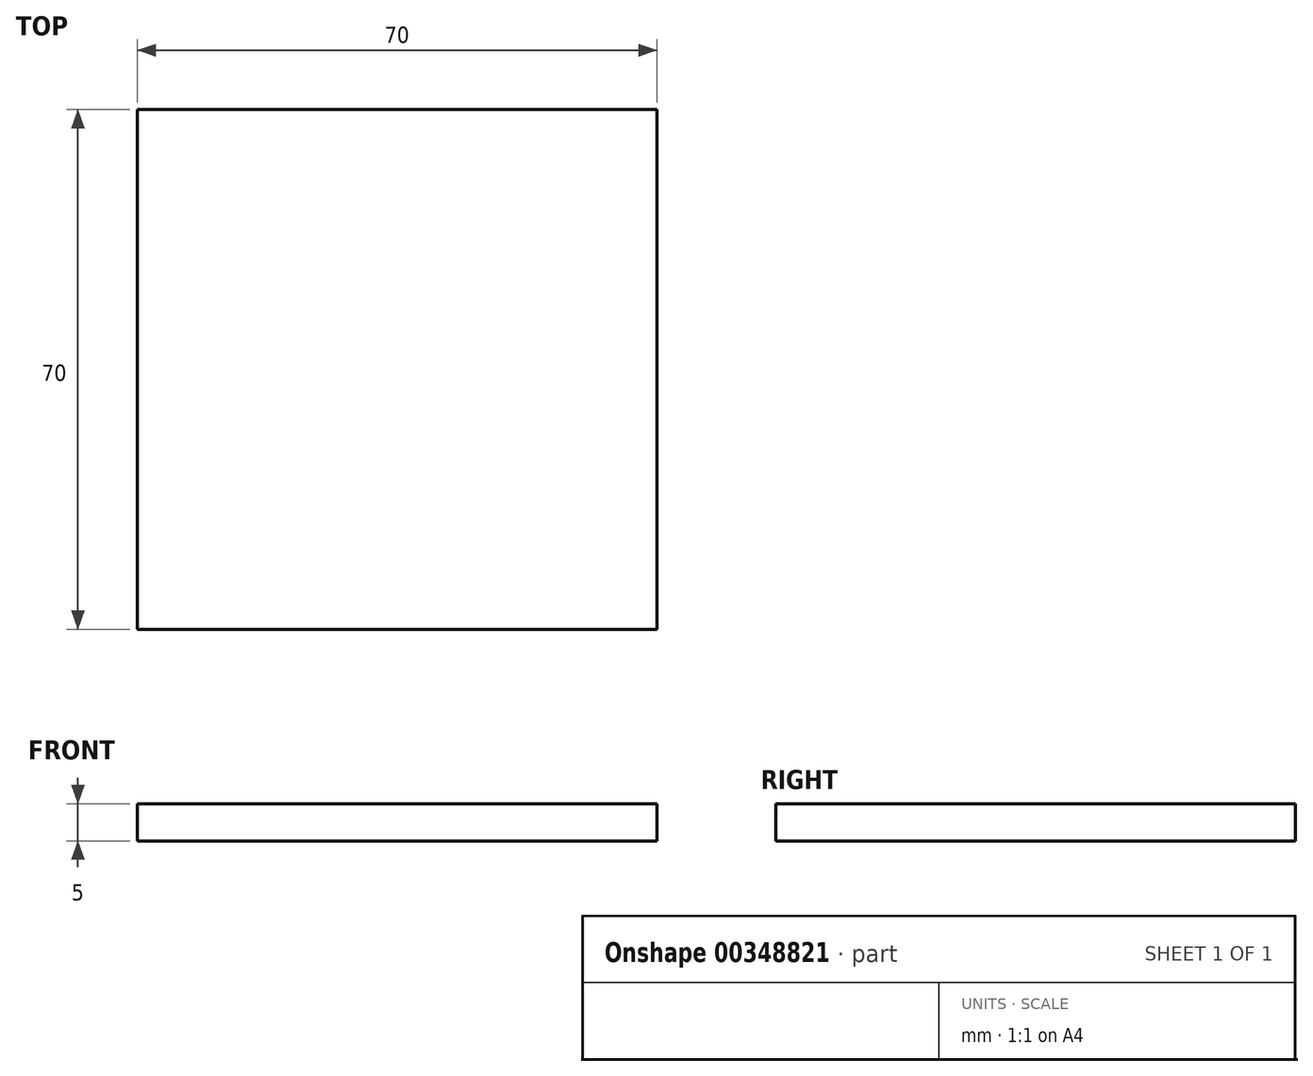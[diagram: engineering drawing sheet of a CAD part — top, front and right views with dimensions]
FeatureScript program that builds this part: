
annotation { "Feature Type Name" : "Feature", "Feature Type Description" : "" }
export const myFeature = defineFeature(function(context is Context, id is Id, definition is map)
    precondition{}
    {
        {
            var Q0;
            Q0=qCreatedBy(makeId("Top.planeOp"),FACE);
            var sketch = newSketch(context, id + "F0", { "sketchPlane" : qUnion([Q0])});
            skLineSegment(sketch, "E0.bottom", {"start": v(-35, 35) * mm, "end": v(35, 35) * mm});
            skLineSegment(sketch, "E0.top", {"start": v(-35, -35) * mm, "end": v(35, -35) * mm});
            skLineSegment(sketch, "E0.left", {"start": v(-35, 35) * mm, "end": v(-35, -35) * mm});
            skLineSegment(sketch, "E0.right", {"start": v(35, 35) * mm, "end": v(35, -35) * mm});
            skSolve(sketch);
        }
        {
            var Q0;
            Q0=makeQuery(id+"F0.imprint","IMPRINT",FACE,{"disambiguationData":[TD([[makeQuery(id+"F0.imprint","IMPRINT",EDGE,{"derivedFrom":sQuery(id+"F0.wireOp",EDGE,"E0.bottom")}),-1.0]])]});
            extrude(context, id + "F1", {"entities" : qUnion([Q0]), "depth" : 5 * mm});
        }
    });
